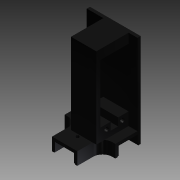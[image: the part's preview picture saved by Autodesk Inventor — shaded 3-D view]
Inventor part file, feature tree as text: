
AUTODESK INVENTOR PART (.ipt)
format: ipt  version: 2015 (Build 190159000, 159)  size: 310,272 bytes
history: native  units: in
note: dims shown in document units (in); Inventor stores cm internally (conversion verified against a paired STEP export)
features: extrude x18, sketch x18, projected_geometry x6, reference x4, other x3, fillet x3, plane x2, split x1
ambient origin geometry x8: Origin, YZ Plane, XZ Plane, XY Plane, X Axis, Y Axis, Z Axis, Center Point
bodies: Solid1 (feature_tree)
feature tree (55):
  extrude  "Extrusion1"  Depth=1.0in
  extrude  "Extrusion2"  Depth=2.0in TaperAngle=0.0deg
  extrude  "Extrusion3"  Depth=0.75in
  extrude  "Extrusion4"  Depth=0.75in TaperAngle=0.0deg
  extrude  "Extrusion5"  Depth=0.75in
  split  "Split1"
  other  "Lip1"
  other  "Lip2"
  other  "Lip3"
  extrude  "Extrusion6"  Depth=0.141in
  fillet  "Fillet1"  Radius=1.0in
  sketch  "Sketch8"  dims[d16=0.03in d17=0.03in d18=0.0in d19=0.0in d20=0.0in d21=0.0in]
  plane  "Work Plane1"
  extrude  "Extrusion7"  Depth=0.125in TaperAngle=0.0deg
  extrude  "Extrusion8"  Depth=1.0in TaperAngle=0.0deg
  extrude  "Extrusion9"  Depth=1.125in TaperAngle=0.0deg
  sketch  "Sketch12"  dims[d37=0.375in d38=0.125in d39=0.0in]
  plane  "Work Plane2"
  extrude  "Extrusion10"  Depth=1.125in TaperAngle=0.0deg
  extrude  "Extrusion11"  Depth=1.0in TaperAngle=0.0deg
  extrude  "Extrusion12"  Depth=0.125in TaperAngle=0.0deg
  extrude  "Extrusion13"  Depth=0.0625in
  extrude  "Extrusion14"  [1 undecoded]
  extrude  "Extrusion15"  [1 undecoded]
  fillet  "Fillet2"  [1 undecoded]
  extrude  "Extrusion16"  [1 undecoded]
  extrude  "Extrusion17"  [1 undecoded]
  fillet  "Fillet3"  [1 undecoded]
  extrude  "Extrusion18"  [1 undecoded]
  sketch  "Sketch1"  dims[d0=1.0in d1=1.0in]
  sketch  "Sketch2"  dims[d2=2.0in d3=0.0in d4=0.5in d5=0.0in]
  sketch  "Sketch4"  dims[d6=0.5in d7=0.0in d8=0.75in]
  sketch  "Sketch5"  dims[d9=0.75in d10=1.75in d11=0.0in]
  sketch  "Sketch6"  dims[d12=0.75in d13=0.75in]
  sketch  "Sketch7"  dims[d14=1.75in d15=0.0in]
  reference  "Reference1"
  sketch  "Sketch9"  dims[d22=0.03in d23=0.03in d24=0.0in d25=0.0in d26=0.0in d27=0.0in]
  projected_geometry  "Projected Loop1"
  sketch  "Sketch11"  dims[d28=0.03in d29=0.03in d30=0.0in d31=0.0in d32=0.0in d33=0.0in d34=0.141in d35=1.0in d36=0.0in]
  projected_geometry  "Projected Loop2"
  projected_geometry  "Projected Loop3"
  sketch  "Sketch13"  dims[d40=1.0in d41=0.0in d42=1.0in d43=0.0in]
  reference  "Reference2"
  sketch  "Sketch14"  dims[d44=1.0in d45=0.0in d46=1.125in d47=0.0in]
  reference  "Reference3"
  sketch  "Sketch15"  dims[d48=1.125in d49=0.0in d50=3.1875in d51=0.0in]
  projected_geometry  "Projected Loop5"
  reference  "Reference4"
  sketch  "Sketch16"  dims[d52=3.1875in d53=0.0in d54=1.0in d55=0.0in]
  sketch  "Sketch17"  dims[d56=0.125in d57=0.125in d58=0.0in]
  sketch  "Sketch19"  dims[d59=0.125in d60=0.0in d61=0.0625in]
  projected_geometry  "Projected Loop6"
  sketch  "Sketch20"  dims[d62=0.125in d63=0.0in]
  projected_geometry  "Projected Loop7"
  sketch  "Sketch21"
note: 7 required parameter values undecoded (feature->parameter linkage not recoverable at this tier; creation-order binding heuristic only, values carry confidence <= 0.55)
